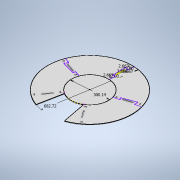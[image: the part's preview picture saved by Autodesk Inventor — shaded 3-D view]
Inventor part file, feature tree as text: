
AUTODESK INVENTOR PART (.ipt)
format: ipt  version: 2020 (Build 240168000, 168)  size: 420,864 bytes
history: native  units: mm
features: extrude x4, sketch x4, pattern_circular x3, mirror x1
ambient origin geometry x8: Origin, YZ Plane, XZ Plane, XY Plane, X Axis, Y Axis, Z Axis, Center Point
bodies: Body1 (feature_tree)
feature tree (12):
  extrude  "Extrusion3"  Depth=6.5mm
  extrude  "Extrusion4"  Depth=2.666667mm
  extrude  "Extrusion5"  Depth=1.333333mm
  sketch  "Sketch5"  dims[d32=1.333333mm d33=1.333333mm]
  extrude  "Extrusion7"  Depth=145.0mm
  pattern_circular  "Circular Pattern2"  Angle=90.0deg  [1 undecoded]
  pattern_circular  "Circular Pattern3"  [2 undecoded]
  mirror  "Mirror3"
  pattern_circular  "Circular Pattern4"  Angle=90.0deg  [1 undecoded]
  sketch  "Sketch2"  dims[d15=6.0mm d16=0.0mm d21=6.5mm]
  sketch  "Sketch3"  dims[d24=2.666667mm d25=2.666667mm]
  sketch  "Sketch6"  dims[d38=0.0mm d39=0.0mm d40=3.25mm d41=90.0deg d42=3.25mm d43=90.0deg d52=4.363323mm d54=10.0mm d55=0.0mm d60=0.872665mm d61=12.566371mm d62=13.439035mm d63=2.666667mm d64=0.523599mm d66=0.523599mm d67=2.666667mm d68=2.666667mm d70=12.566371mm d71=12.566371mm d84=300.14mm d85=682.72mm d86=491.43mm d87=150.07mm d88=341.36mm d89=4.363323mm d90=1.919862mm d91=1.919862mm d94=300.14mm d95=682.72mm d104=6.5mm d105=12.0mm d108=1.333333mm d109=1.333333mm d110=1.333333mm d111=1.333333mm d112=0.0mm d113=0.0mm d114=0.0mm d145=20.0mm d146=12.566371mm d149=145.0mm d150=90.0deg d151=90.0deg d152=90.0deg d153=90.0deg d154=20.0mm d155=25.132741mm d157=20.0mm d158=25.132741mm]
note: 4 required parameter values undecoded (feature->parameter linkage not recoverable at this tier; creation-order binding heuristic only, values carry confidence <= 0.55)
